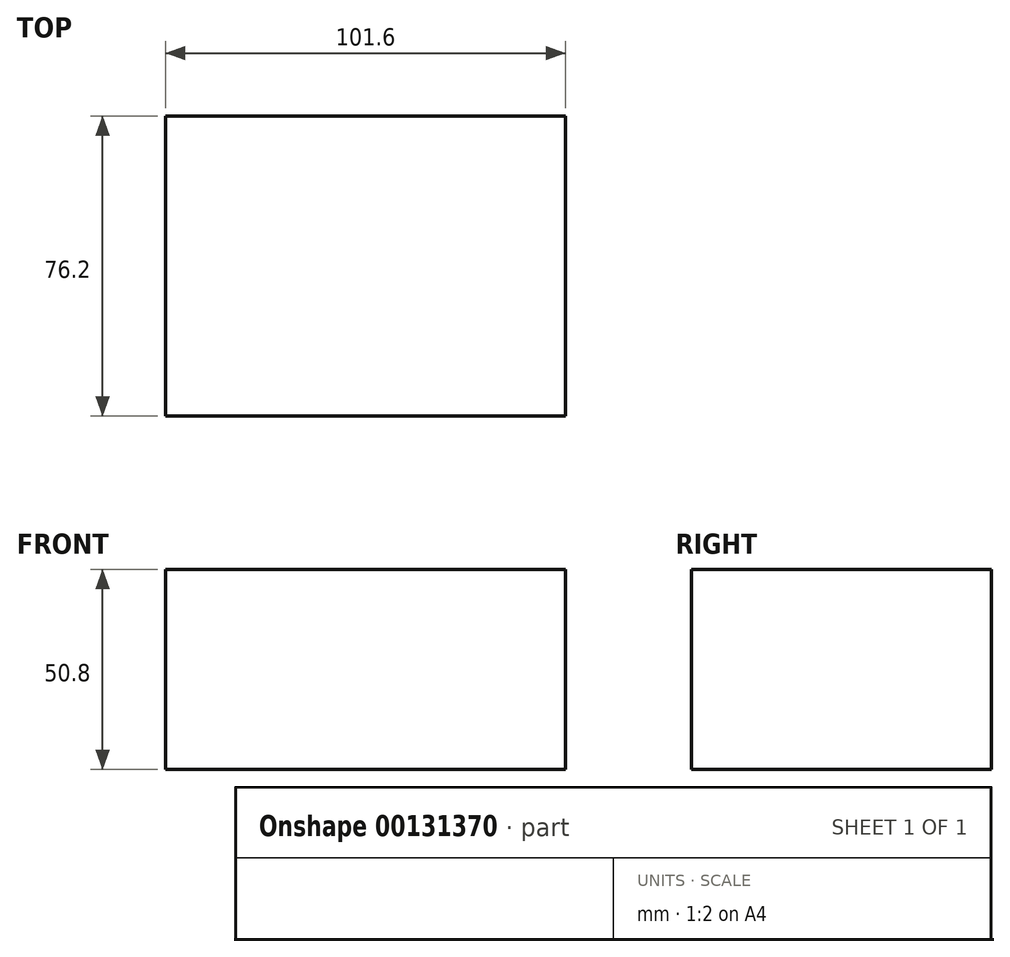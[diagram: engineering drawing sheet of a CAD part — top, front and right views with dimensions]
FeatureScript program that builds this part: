
annotation { "Feature Type Name" : "Feature", "Feature Type Description" : "" }
export const myFeature = defineFeature(function(context is Context, id is Id, definition is map)
    precondition{}
    {
        {
            var Q0;
            Q0=qCreatedBy(makeId("Front.planeOp"),FACE);
            var sketch = newSketch(context, id + "F0", { "sketchPlane" : qUnion([Q0])});
            skLineSegment(sketch, "E0.bottom", {"start": v(50.8, 25.4) * mm, "end": v(-50.8, 25.4) * mm});
            skLineSegment(sketch, "E0.top", {"start": v(50.8, -25.4) * mm, "end": v(-50.8, -25.4) * mm});
            skLineSegment(sketch, "E0.left", {"start": v(50.8, 25.4) * mm, "end": v(50.8, -25.4) * mm});
            skLineSegment(sketch, "E0.right", {"start": v(-50.8, 25.4) * mm, "end": v(-50.8, -25.4) * mm});
            skPoint(sketch, "E0.middle", {"position": v(0, 0) * mm});
            skSolve(sketch);
        }
        {
            var Q0;
            Q0 = qSketchRegion(id + "F0", true);
            extrude(context, id + "F1", {"entities" : qUnion([Q0]), "depth" : 76.2 * mm});
        }
    });
